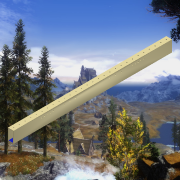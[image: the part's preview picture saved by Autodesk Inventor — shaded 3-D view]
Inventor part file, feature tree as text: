
AUTODESK INVENTOR PART (.ipt)
format: ipt  version: 2,015 SP1 (Build 190203100, 203)  size: 1,586,688 bytes
history: native  units: in
note: dims shown in document units (in); Inventor stores cm internally (conversion verified against a paired STEP export)
features: projected_geometry x16, sketch x7, extrude x5, reference x5, plane x3, other x2, hole x2, fillet x1, imported_body x1
ambient origin geometry x8: Origin, YZ Plane, XZ Plane, XY Plane, X Axis, Y Axis, Z Axis, Center Point
bodies: Body1 (feature_tree)
feature tree (42):
  other  "Cut-Extrude2"
  other  "1 x 2 x 0.10 Pre-Drilled Tube Stock (59 length)1"
  plane  "Work Plane1"
  extrude  "Extrusion1"  Depth=1.0in TaperAngle=0.0deg
  plane  "Work Plane5"
  sketch  "Sketch5"  dims[d22=1.0in d24=0.25in]
  plane  "Work Plane6"
  hole  "Hole2"  [1 undecoded]
  hole  "Hole4"  [1 undecoded]
  extrude  "Extrusion5"  Depth=1.0in
  extrude  "Extrusion6"  Depth=0.1in TaperAngle=0.0deg
  extrude  "Extrusion7"  Depth=0.1in TaperAngle=0.0deg
  extrude  "Extrusion8"  Depth=0.1in TaperAngle=0.0deg
  fillet  "Fillet1"  Radius=0.0625in
  imported_body  "Base1"
  sketch  "Sketch1"  dims[d0=28.0in d1=1.0in d2=0.0in]
  sketch  "Sketch6"  dims[d27=11.5in d28=4.0in]
  reference  "Reference1"
  reference  "Reference2"
  sketch  "Sketch10"  dims[d29=0.163in d30=0.75in d31=0.375in d32=0.25in d33=0.5635in d34=1.0in d35=0.8108in]
  reference  "Reference7"
  reference  "Reference8"
  reference  "Reference9"
  sketch  "Sketch13"  dims[d63=0.163in d64=0.75in d65=0.375in d66=0.25in d67=0.5635in d68=1.0in d69=0.8108in d70=1.0in]
  projected_geometry  "Projected Loop43"
  projected_geometry  "Projected Loop44"
  projected_geometry  "Projected Loop45"
  projected_geometry  "Projected Loop46"
  projected_geometry  "Projected Loop47"
  projected_geometry  "Projected Loop48"
  projected_geometry  "Projected Loop49"
  projected_geometry  "Projected Loop50"
  projected_geometry  "Projected Loop51"
  projected_geometry  "Projected Loop52"
  sketch  "Sketch14"  dims[d71=1.0in d72=0.1in d73=0.0in]
  projected_geometry  "Projected Loop53"
  projected_geometry  "Projected Loop54"
  sketch  "Sketch15"  dims[d74=0.4in d75=0.0in d76=0.1in d77=0.0in d78=0.1in d79=0.0in d80=0.0625in]
  projected_geometry  "Projected Loop55"
  projected_geometry  "Projected Loop56"
  projected_geometry  "Projected Loop57"
  projected_geometry  "Projected Loop58"
note: 2 required parameter values undecoded (feature->parameter linkage not recoverable at this tier; creation-order binding heuristic only, values carry confidence <= 0.55)
